# Revit family: Tall Choral Folio Cabinet
name_source: partatom
category: Furniture
revit_build: Autodesk Revit Architecture 2012 (Build: 20110916_2132(x64)
units: mm (PartAtom-declared; Revit-internal decimal feet)

## types (4) — shared parameters
Manufacturer = Wenger Corporation
URL = http://www.wengercorp.com

## per-type parameters (varying)
| type | Cabinet Back Thickness | Cabinet Depth | Cabinet Height | Cabinet Label | Cabinet Width | Model | Thickness Wood |
| Standard Cabinet #60 | 3/4" | 19 1/4" | 84" | Labels : Standard | 24 5/8" | 60 | 3/4" |
| Acoustic Cabinet #60 | 3 1/4" | 31 3/4" | 38 5/16" | Labels : Acoustic | 18 3/4" | 60A | 95/128" |
| Narrow Acoustic Cabinet #60 | 3 1/4" | 31 3/4" | 38 5/16" | Labels : Narrow Acoustic | 14 3/4" | 60NA | 95/128" |
| Narrow Cabinet #60 | 3/4" | 29 1/4" | 38 5/16" | Labels : Narrow | 14 3/4" | 60N | 95/128" |

note: column(s) folded — value = type name in every type: Description

## geometry (parser evidence)
native form markers: Blend x10, Sweep x4
no freeform markers — native parametric forms only
